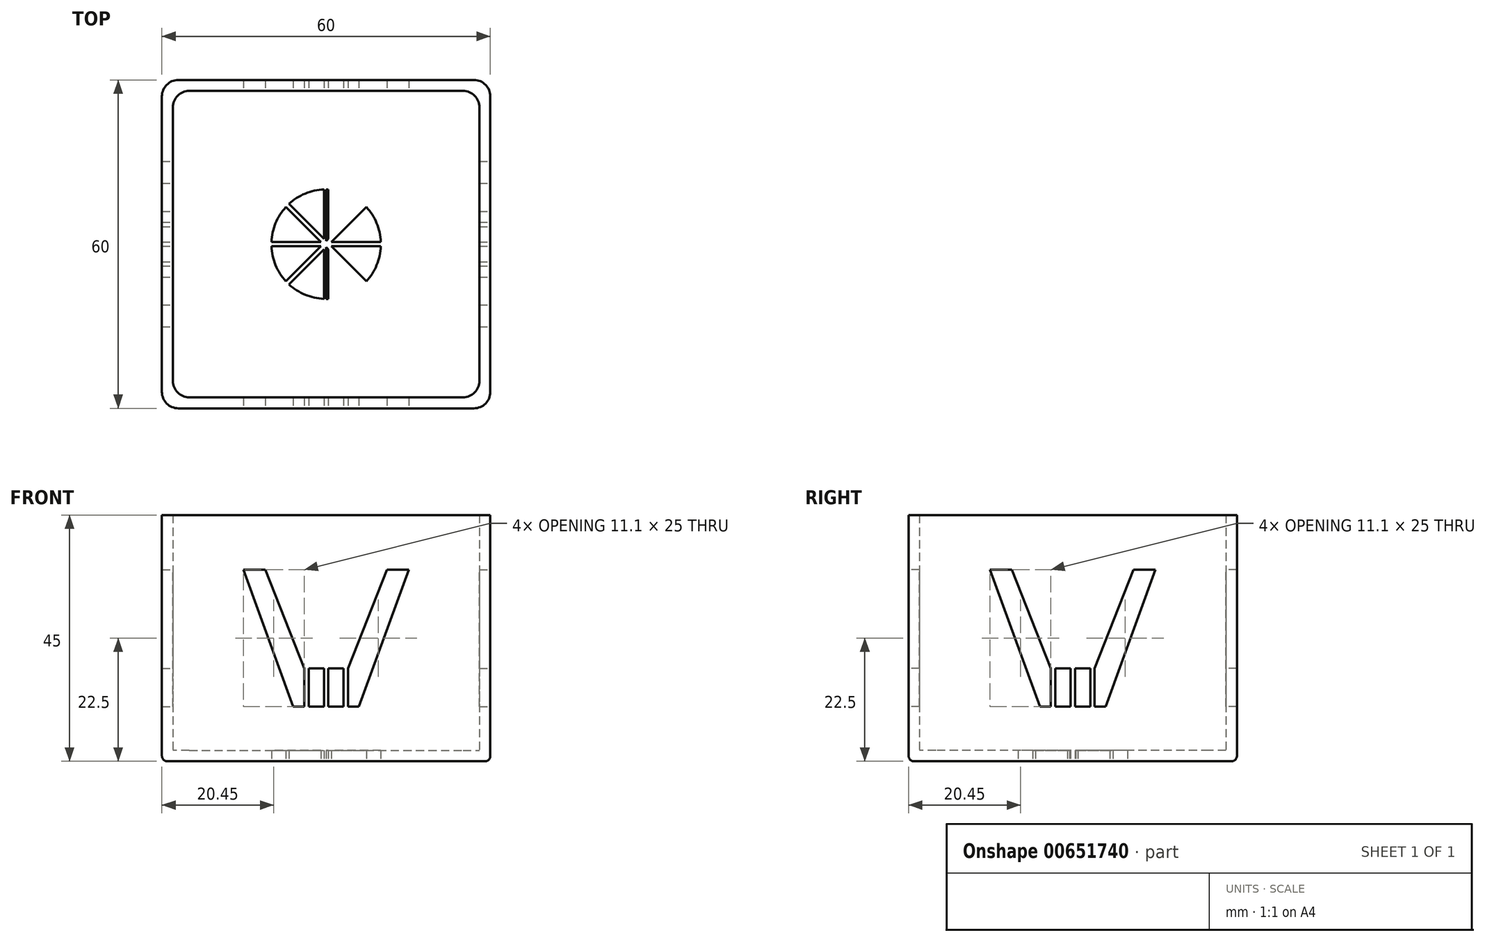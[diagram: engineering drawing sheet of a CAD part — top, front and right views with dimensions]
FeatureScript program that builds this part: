
annotation { "Feature Type Name" : "Feature", "Feature Type Description" : "" }
export const myFeature = defineFeature(function(context is Context, id is Id, definition is map)
    precondition{}
    {
        {
            var Q0;
            Q0=qCreatedBy(makeId("Top.planeOp"),FACE);
            var sketch = newSketch(context, id + "F0", { "sketchPlane" : qUnion([Q0])});
            skLineSegment(sketch, "E0.bottom", {"start": v(-30, 30) * mm, "end": v(30, 30) * mm});
            skLineSegment(sketch, "E0.top", {"start": v(-30, -30) * mm, "end": v(30, -30) * mm});
            skLineSegment(sketch, "E0.left", {"start": v(-30, 30) * mm, "end": v(-30, -30) * mm});
            skLineSegment(sketch, "E0.right", {"start": v(30, 30) * mm, "end": v(30, -30) * mm});
            skSolve(sketch);
        }
        {
            var Q0;
            Q0=makeQuery(id+"F0.imprint","IMPRINT",FACE,{"disambiguationData":[TD([[makeQuery(id+"F0.imprint","IMPRINT",EDGE,{"derivedFrom":sQuery(id+"F0.wireOp",EDGE,"E0.bottom")}),-1.0]])]});
            var Q1;
            Q1=qSketchRegion(id+"F3",true);
            extrude(context, id + "F1", {"entities" : qUnion([Q0, Q1]), "depth" : 45 * mm, "offsetDistance" : 25 * mm});
        }
        {
            var Q0;
            Q0=makeQuery(id+"F1.opExtrude","CAP_FACE",FACE,{"disambiguationData":[OSD([sQuery(id+"F0.wireOp",EDGE,"E0.bottom"),sQuery(id+"F0.wireOp",EDGE,"E0.top"),sQuery(id+"F0.wireOp",EDGE,"E0.left"),sQuery(id+"F0.wireOp",EDGE,"E0.right")])],"isStart":false});
            shell(context, id + "F2", {"entities" : qUnion([Q0]), "thickness" : 2 * mm});
        }
        {
            var Q0;
            Q0=makeQuery(id+"F1.opExtrude","SWEPT_FACE",FACE,{"disambiguationData":[OSD([sQuery(id+"F0.wireOp",EDGE,"E0.top")])]});
            var sketch = newSketch(context, id + "F3", { "sketchPlane" : qUnion([Q0])});
            skLineSegment(sketch, "E1", {"start": v(-6, 10) * mm, "end": v(6, 10) * mm});
            skLineSegment(sketch, "E2", {"start": v(6, 10) * mm, "end": v(15.1, 35) * mm});
            skLineSegment(sketch, "E3", {"start": v(-6, 10) * mm, "end": v(-15.1, 35) * mm});
            skLineSegment(sketch, "E4", {"start": v(15.1, 35) * mm, "end": v(15.1, 45) * mm});
            skLineSegment(sketch, "E5", {"start": v(-15.1, 35) * mm, "end": v(-11.1, 35) * mm});
            skLineSegment(sketch, "E6", {"start": v(15.1, 35) * mm, "end": v(11.1, 35) * mm});
            skLineSegment(sketch, "E7", {"start": v(-11.1, 35) * mm, "end": v(-4, 17) * mm});
            skLineSegment(sketch, "E8", {"start": v(11.1, 35) * mm, "end": v(4, 17) * mm});
            skLineSegment(sketch, "E9", {"start": v(-4, 17) * mm, "end": v(4, 17) * mm});
            skLineSegment(sketch, "E10", {"start": v(-4, 17) * mm, "end": v(-4, 10) * mm});
            skLineSegment(sketch, "E11", {"start": v(-3.2, 17) * mm, "end": v(-3.2, 10) * mm});
            skLineSegment(sketch, "E12", {"start": v(4, 17) * mm, "end": v(4, 10) * mm});
            skLineSegment(sketch, "E13", {"start": v(3.2, 17) * mm, "end": v(3.2, 10) * mm});
            skLineSegment(sketch, "E14", {"start": v(0, 17) * mm, "end": v(0, 10) * mm});
            skLineSegment(sketch, "E15", {"start": v(0.4, 17) * mm, "end": v(0.4, 10) * mm});
            skLineSegment(sketch, "E16", {"start": v(-0.4, 17) * mm, "end": v(-0.4, 10) * mm});
            skSolve(sketch);
        }
        {
            var Q0;
            {var subQ0=sQuery(id+"F3.wireOp",EDGE,"E3");Q0=makeQuery(id+"F3.imprint","IMPRINT",FACE,{"disambiguationData":[TD([[makeQuery(id+"F3.imprint","IMPRINT",EDGE,{"derivedFrom":subQ0}),-1.0]])]});}
            var Q1;
            {var subQ0=sQuery(id+"F3.wireOp",EDGE,"E11");Q1=makeQuery(id+"F3.imprint","IMPRINT",FACE,{"disambiguationData":[TD([[makeQuery(id+"F3.imprint","IMPRINT",EDGE,{"derivedFrom":subQ0}),1.0]])]});}
            var Q2;
            {var subQ0=sQuery(id+"F3.wireOp",EDGE,"E13");Q2=makeQuery(id+"F3.imprint","IMPRINT",FACE,{"disambiguationData":[TD([[makeQuery(id+"F3.imprint","IMPRINT",EDGE,{"derivedFrom":subQ0}),-1.0]])]});}
            var Q3;
            {var subQ1=sQuery(id+"F3.wireOp",EDGE,"E2");Q3=makeQuery(id+"F3.imprint","IMPRINT",FACE,{"disambiguationData":[TD([[makeQuery(id+"F3.imprint","IMPRINT",EDGE,{"derivedFrom":subQ1}),1.0]])]});}
            extrude(context, id + "F4", {"entities" : qUnion([Q0, Q1, Q2, Q3]), "operationType" : NewBodyOperationType.REMOVE, "oppositeDirection" : true, "depth" : 64.2 * mm, "offsetDistance" : 25 * mm});
        }
        {
            var Q0;
            Q0=makeQuery(id+"F1.opExtrude","SWEPT_FACE",FACE,{"disambiguationData":[OSD([sQuery(id+"F0.wireOp",EDGE,"E0.right")])]});
            var sketch = newSketch(context, id + "F5", { "sketchPlane" : qUnion([Q0])});
            skLineSegment(sketch, "E17", {"start": v(-6, 10) * mm, "end": v(6, 10) * mm});
            skLineSegment(sketch, "E18", {"start": v(6, 10) * mm, "end": v(15.1, 35) * mm});
            skLineSegment(sketch, "E19", {"start": v(-6, 10) * mm, "end": v(-15.1, 35) * mm});
            skLineSegment(sketch, "E20", {"start": v(-15.1, 35) * mm, "end": v(-11.1, 35) * mm});
            skLineSegment(sketch, "E21", {"start": v(15.1, 35) * mm, "end": v(11.1, 35) * mm});
            skLineSegment(sketch, "E22", {"start": v(-11.1, 35) * mm, "end": v(-4, 17) * mm});
            skLineSegment(sketch, "E23", {"start": v(11.1, 35) * mm, "end": v(4, 17) * mm});
            skLineSegment(sketch, "E24", {"start": v(-4, 17) * mm, "end": v(4, 17) * mm});
            skLineSegment(sketch, "E25", {"start": v(-4, 17) * mm, "end": v(-4, 10) * mm});
            skLineSegment(sketch, "E26", {"start": v(-3.2, 17) * mm, "end": v(-3.2, 10) * mm});
            skLineSegment(sketch, "E27", {"start": v(4, 17) * mm, "end": v(4, 10) * mm});
            skLineSegment(sketch, "E28", {"start": v(3.2, 17) * mm, "end": v(3.2, 10) * mm});
            skLineSegment(sketch, "E29", {"start": v(0, 17) * mm, "end": v(0, 10) * mm});
            skLineSegment(sketch, "E30", {"start": v(0.4, 17) * mm, "end": v(0.4, 10) * mm});
            skLineSegment(sketch, "E31", {"start": v(-0.4, 17) * mm, "end": v(-0.4, 10) * mm});
            skLineSegment(sketch, "E32", {"start": v(15.1, 35) * mm, "end": v(15.1, 45) * mm});
            skSolve(sketch);
        }
        {
            var Q0;
            {var subQ0=sQuery(id+"F5.wireOp",EDGE,"E19");Q0=makeQuery(id+"F5.imprint","IMPRINT",FACE,{"disambiguationData":[TD([[makeQuery(id+"F5.imprint","IMPRINT",EDGE,{"derivedFrom":subQ0}),-1.0]])]});}
            var Q1;
            {var subQ0=sQuery(id+"F5.wireOp",EDGE,"E26");Q1=makeQuery(id+"F5.imprint","IMPRINT",FACE,{"disambiguationData":[TD([[makeQuery(id+"F5.imprint","IMPRINT",EDGE,{"derivedFrom":subQ0}),1.0]])]});}
            var Q2;
            {var subQ0=sQuery(id+"F5.wireOp",EDGE,"E28");Q2=makeQuery(id+"F5.imprint","IMPRINT",FACE,{"disambiguationData":[TD([[makeQuery(id+"F5.imprint","IMPRINT",EDGE,{"derivedFrom":subQ0}),-1.0]])]});}
            var Q3;
            {var subQ1=sQuery(id+"F5.wireOp",EDGE,"E18");Q3=makeQuery(id+"F5.imprint","IMPRINT",FACE,{"disambiguationData":[TD([[makeQuery(id+"F5.imprint","IMPRINT",EDGE,{"derivedFrom":subQ1}),1.0]])]});}
            extrude(context, id + "F6", {"entities" : qUnion([Q0, Q1, Q2, Q3]), "operationType" : NewBodyOperationType.REMOVE, "oppositeDirection" : true, "depth" : 63.5 * mm, "offsetDistance" : 25 * mm});
        }
        {
            var Q0;
            Q0=makeQuery(id+"F1.opExtrude","CAP_FACE",FACE,{"disambiguationData":[OSD([sQuery(id+"F0.wireOp",EDGE,"E0.bottom"),sQuery(id+"F0.wireOp",EDGE,"E0.top"),sQuery(id+"F0.wireOp",EDGE,"E0.left"),sQuery(id+"F0.wireOp",EDGE,"E0.right")])],"isStart":true});
            var sketch = newSketch(context, id + "F7", { "sketchPlane" : qUnion([Q0])});
            skCircle(sketch, "E33", {"center": v(0, 0) * mm, "radius": 10 * mm});
            skLineSegment(sketch, "E34", {"start": v(0, 10) * mm, "end": v(0, -10) * mm});
            skLineSegment(sketch, "E35", {"start": v(-10, 0) * mm, "end": v(10, 0) * mm});
            skLineSegment(sketch, "E36", {"start": v(-10, -0.4) * mm, "end": v(10, -0.4) * mm});
            skLineSegment(sketch, "E37", {"start": v(-10, 0.4) * mm, "end": v(10, 0.4) * mm});
            skLineSegment(sketch, "E38", {"start": v(0.4, 10) * mm, "end": v(0.4, -10) * mm});
            skLineSegment(sketch, "E39", {"start": v(-0.4, 10) * mm, "end": v(-0.4, -10) * mm});
            skLineSegment(sketch, "E40", {"start": v(-7.07, -7.07) * mm, "end": v(7.07, 7.07) * mm});
            skLineSegment(sketch, "E41", {"start": v(7.07, -7.07) * mm, "end": v(-7.07, 7.07) * mm});
            skLineSegment(sketch, "E42", {"start": v(-6.78, -7.35) * mm, "end": v(7.35, 6.78) * mm});
            skLineSegment(sketch, "E43", {"start": v(-7.35, -6.78) * mm, "end": v(6.78, 7.35) * mm});
            skLineSegment(sketch, "E44", {"start": v(6.78, -7.35) * mm, "end": v(-7.35, 6.78) * mm});
            skLineSegment(sketch, "E45", {"start": v(7.35, -6.78) * mm, "end": v(-6.78, 7.35) * mm});
            skSolve(sketch);
        }
        {
            var Q0;
            {var subQ0=sQuery(id+"F7.wireOp",EDGE,"E39");var subQ1=sQuery(id+"F7.wireOp",EDGE,"E33");var subQ2=makeQuery(id+"F7.imprint","INTERSECT",VERTEX,{"disambiguationData":[OD(0.0)],"derivedFrom":[subQ1,subQ0]});Q0=makeQuery(id+"F7.imprint","IMPRINT",FACE,{"disambiguationData":[TD([[makeQuery(id+"F7.imprint","IMPRINT",EDGE,{"disambiguationData":[TD([[subQ2,-1.0]])],"derivedFrom":subQ1}),1.0]])]});}
            var Q1;
            {var subQ0=sQuery(id+"F7.wireOp",EDGE,"E38");var subQ1=sQuery(id+"F7.wireOp",EDGE,"E33");var subQ2=makeQuery(id+"F7.imprint","INTERSECT",VERTEX,{"disambiguationData":[OD(0.0)],"derivedFrom":[subQ1,subQ0]});Q1=makeQuery(id+"F7.imprint","IMPRINT",FACE,{"disambiguationData":[TD([[makeQuery(id+"F7.imprint","IMPRINT",EDGE,{"disambiguationData":[TD([[subQ2,1.0]])],"derivedFrom":subQ1}),1.0]])]});}
            var Q2;
            {var subQ0=sQuery(id+"F7.wireOp",EDGE,"E37");var subQ1=sQuery(id+"F7.wireOp",EDGE,"E33");var subQ2=makeQuery(id+"F7.imprint","INTERSECT",VERTEX,{"disambiguationData":[OD(1.0)],"derivedFrom":[subQ1,subQ0]});Q2=makeQuery(id+"F7.imprint","IMPRINT",FACE,{"disambiguationData":[TD([[makeQuery(id+"F7.imprint","IMPRINT",EDGE,{"disambiguationData":[TD([[subQ2,-1.0]])],"derivedFrom":subQ1}),1.0]])]});}
            var Q3;
            {var subQ0=sQuery(id+"F7.wireOp",EDGE,"E36");var subQ1=sQuery(id+"F7.wireOp",EDGE,"E33");var subQ2=makeQuery(id+"F7.imprint","INTERSECT",VERTEX,{"disambiguationData":[OD(1.0)],"derivedFrom":[subQ1,subQ0]});Q3=makeQuery(id+"F7.imprint","IMPRINT",FACE,{"disambiguationData":[TD([[makeQuery(id+"F7.imprint","IMPRINT",EDGE,{"disambiguationData":[TD([[subQ2,1.0]])],"derivedFrom":subQ1}),1.0]])]});}
            var Q4;
            {var subQ0=sQuery(id+"F7.wireOp",EDGE,"E38");var subQ1=sQuery(id+"F7.wireOp",EDGE,"E33");var subQ2=makeQuery(id+"F7.imprint","INTERSECT",VERTEX,{"disambiguationData":[OD(1.0)],"derivedFrom":[subQ1,subQ0]});Q4=makeQuery(id+"F7.imprint","IMPRINT",FACE,{"disambiguationData":[TD([[makeQuery(id+"F7.imprint","IMPRINT",EDGE,{"disambiguationData":[TD([[subQ2,-1.0]])],"derivedFrom":subQ1}),1.0]])]});}
            var Q5;
            {var subQ0=sQuery(id+"F7.wireOp",EDGE,"E39");var subQ1=sQuery(id+"F7.wireOp",EDGE,"E33");var subQ2=makeQuery(id+"F7.imprint","INTERSECT",VERTEX,{"disambiguationData":[OD(1.0)],"derivedFrom":[subQ1,subQ0]});Q5=makeQuery(id+"F7.imprint","IMPRINT",FACE,{"disambiguationData":[TD([[makeQuery(id+"F7.imprint","IMPRINT",EDGE,{"disambiguationData":[TD([[subQ2,1.0]])],"derivedFrom":subQ1}),1.0]])]});}
            var Q6;
            {var subQ0=sQuery(id+"F7.wireOp",EDGE,"E36");var subQ1=sQuery(id+"F7.wireOp",EDGE,"E33");var subQ2=makeQuery(id+"F7.imprint","INTERSECT",VERTEX,{"disambiguationData":[OD(0.0)],"derivedFrom":[subQ1,subQ0]});Q6=makeQuery(id+"F7.imprint","IMPRINT",FACE,{"disambiguationData":[TD([[makeQuery(id+"F7.imprint","IMPRINT",EDGE,{"disambiguationData":[TD([[subQ2,-1.0]])],"derivedFrom":subQ1}),1.0]])]});}
            var Q7;
            {var subQ0=sQuery(id+"F7.wireOp",EDGE,"E37");var subQ1=sQuery(id+"F7.wireOp",EDGE,"E33");var subQ2=makeQuery(id+"F7.imprint","INTERSECT",VERTEX,{"disambiguationData":[OD(0.0)],"derivedFrom":[subQ1,subQ0]});Q7=makeQuery(id+"F7.imprint","IMPRINT",FACE,{"disambiguationData":[TD([[makeQuery(id+"F7.imprint","IMPRINT",EDGE,{"disambiguationData":[TD([[subQ2,1.0]])],"derivedFrom":subQ1}),1.0]])]});}
            extrude(context, id + "F8", {"entities" : qUnion([Q0, Q1, Q2, Q3, Q4, Q5, Q6, Q7]), "operationType" : NewBodyOperationType.REMOVE, "oppositeDirection" : true, "depth" : 25 * mm, "offsetDistance" : 25 * mm});
        }
        {
            var Q0;
            Q0=makeQuery(id+"F1.opExtrude","SWEPT_EDGE",EDGE,{"disambiguationData":[OSD([sQuery(id+"F0.wireOp",EDGE,"E0.top"),sQuery(id+"F0.wireOp",EDGE,"E0.left")])]});
            var Q1;
            Q1=makeQuery(id+"F1.opExtrude","SWEPT_EDGE",EDGE,{"disambiguationData":[OSD([sQuery(id+"F0.wireOp",EDGE,"E0.top"),sQuery(id+"F0.wireOp",EDGE,"E0.right")])]});
            var Q2;
            Q2=makeQuery(id+"F1.opExtrude","SWEPT_EDGE",EDGE,{"disambiguationData":[OSD([sQuery(id+"F0.wireOp",EDGE,"E0.bottom"),sQuery(id+"F0.wireOp",EDGE,"E0.right")])]});
            var Q3;
            Q3=makeQuery(id+"F1.opExtrude","SWEPT_EDGE",EDGE,{"disambiguationData":[OSD([sQuery(id+"F0.wireOp",EDGE,"E0.bottom"),sQuery(id+"F0.wireOp",EDGE,"E0.left")])]});
            var Q4;
            Q4=makeQuery(id+"F2.opShell","OFFSET_EDGE",EDGE,{"disambiguationData":[OSD([sQuery(id+"F0.wireOp",EDGE,"E0.top"),sQuery(id+"F0.wireOp",EDGE,"E0.left")])]});
            var Q5;
            Q5=makeQuery(id+"F2.opShell","OFFSET_EDGE",EDGE,{"disambiguationData":[OSD([sQuery(id+"F0.wireOp",EDGE,"E0.top"),sQuery(id+"F0.wireOp",EDGE,"E0.right")])]});
            var Q6;
            Q6=makeQuery(id+"F2.opShell","OFFSET_EDGE",EDGE,{"disambiguationData":[OSD([sQuery(id+"F0.wireOp",EDGE,"E0.bottom"),sQuery(id+"F0.wireOp",EDGE,"E0.right")])]});
            var Q7;
            Q7=makeQuery(id+"F2.opShell","OFFSET_EDGE",EDGE,{"disambiguationData":[OSD([sQuery(id+"F0.wireOp",EDGE,"E0.bottom"),sQuery(id+"F0.wireOp",EDGE,"E0.left")])]});
            fillet(context, id + "F9", {"entities" : qUnion([Q0, Q1, Q2, Q3, Q4, Q5, Q6, Q7]), "radius" : 3 * mm, "tangentPropagation" : true, "allowEdgeOverflow" : false});
        }
        {
            var Q0;
            Q0=makeQuery(id+"F1.opExtrude","CAP_EDGE",EDGE,{"disambiguationData":[OSD([sQuery(id+"F0.wireOp",EDGE,"E0.top")])],"isStart":true});
            var Q1;
            Q1=makeQuery(id+"F1.opExtrude","CAP_EDGE",EDGE,{"disambiguationData":[OSD([sQuery(id+"F0.wireOp",EDGE,"E0.left")])],"isStart":true});
            var Q2;
            Q2=makeQuery(id+"F1.opExtrude","CAP_EDGE",EDGE,{"disambiguationData":[OSD([sQuery(id+"F0.wireOp",EDGE,"E0.right")])],"isStart":true});
            var Q3;
            Q3=makeQuery(id+"F1.opExtrude","CAP_EDGE",EDGE,{"disambiguationData":[OSD([sQuery(id+"F0.wireOp",EDGE,"E0.bottom")])],"isStart":true});
            fillet(context, id + "F10", {"entities" : qUnion([Q0, Q1, Q2, Q3]), "radius" : 1 * mm, "tangentPropagation" : true, "allowEdgeOverflow" : false});
        }
    });
